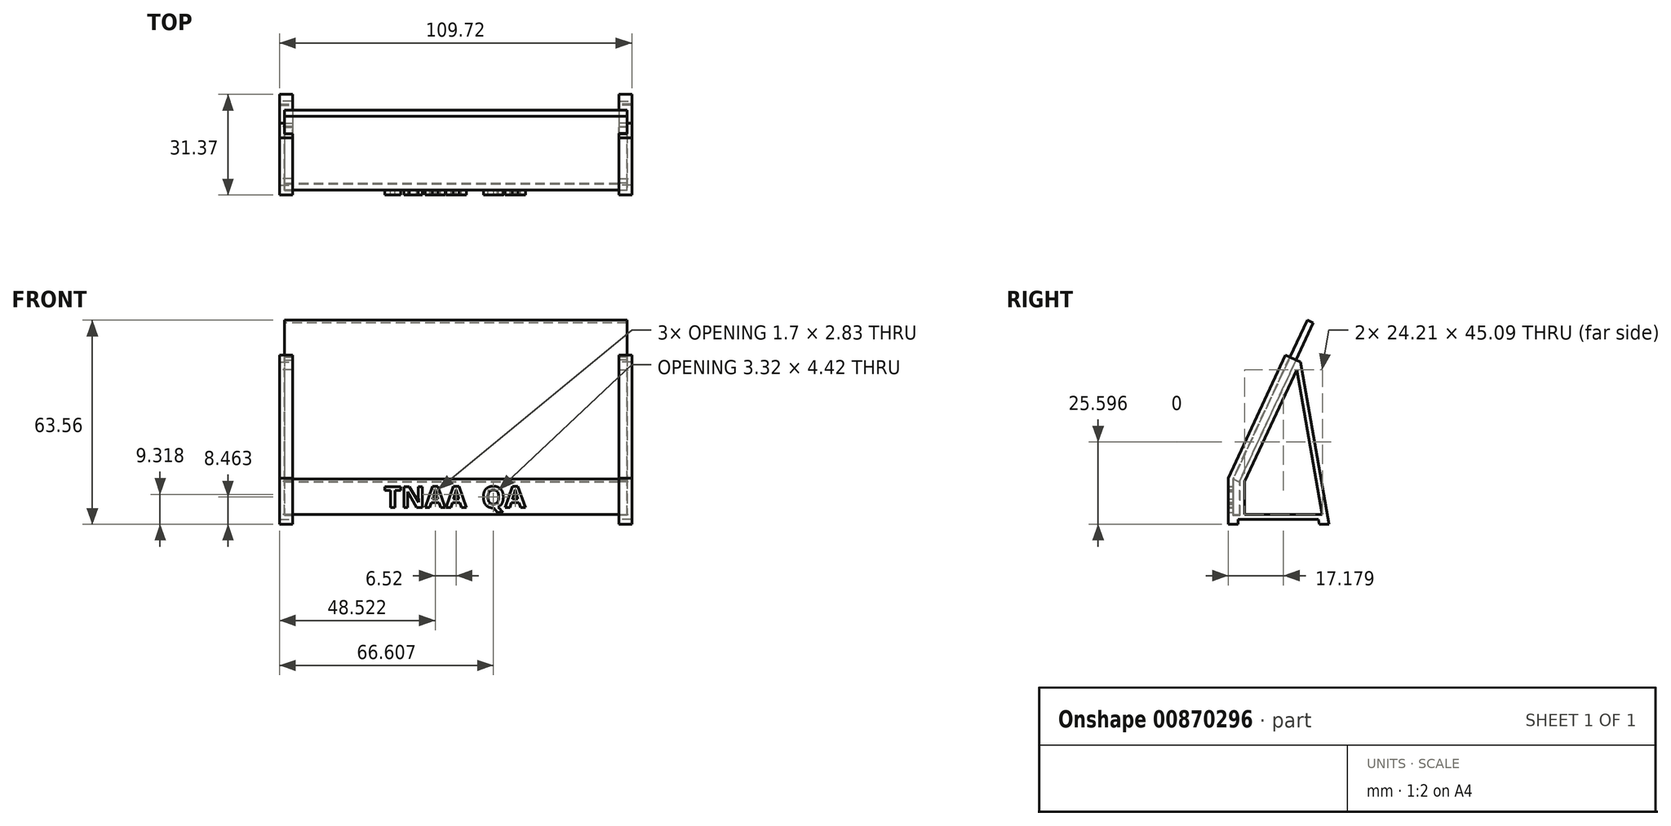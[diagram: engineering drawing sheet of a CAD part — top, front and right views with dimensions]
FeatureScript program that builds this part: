
annotation { "Feature Type Name" : "Feature", "Feature Type Description" : "" }
export const myFeature = defineFeature(function(context is Context, id is Id, definition is map)
    precondition{}
    {
        {
            var Q0;
            Q0=qCreatedBy(makeId("Right.planeOp"),FACE);
            var sketch = newSketch(context, id + "F0", { "sketchPlane" : qUnion([Q0])});
            skLineSegment(sketch, "E0", {"start": v(0, 49.5) * mm, "end": v(-23.08, 0) * mm});
            skLineSegment(sketch, "E1", {"start": v(0, 49.5) * mm, "end": v(-1.84, 50.35) * mm});
            skLineSegment(sketch, "E2", {"start": v(-1.84, 50.35) * mm, "end": v(-24.92, 0.86) * mm});
            skLineSegment(sketch, "E3", {"start": v(-24.92, 0.86) * mm, "end": v(-23.08, 0) * mm});
            skSolve(sketch);
        }
        {
            var Q0;
            Q0=qCreatedBy(makeId("Right.planeOp"),FACE);
            var sketch = newSketch(context, id + "F1", { "sketchPlane" : qUnion([Q0])});
            skLineSegment(sketch, "E4", {"start": v(-22.89, -0.09) * mm, "end": v(-24.92, 0.86) * mm});
            skLineSegment(sketch, "E5", {"start": v(-24.92, 0.86) * mm, "end": v(-24.92, -10.16) * mm});
            skLineSegment(sketch, "E6", {"start": v(-24.92, -10.16) * mm, "end": v(-22.89, -10.16) * mm});
            skLineSegment(sketch, "E7", {"start": v(-22.89, -10.16) * mm, "end": v(-22.89, -0.09) * mm});
            skSolve(sketch);
        }
        {
            var Q0;
            Q0=makeQuery(id+"F1.imprint","IMPRINT",FACE,{"disambiguationData":[TD([[makeQuery(id+"F1.imprint","IMPRINT",EDGE,{"derivedFrom":sQuery(id+"F1.wireOp",EDGE,"E4")}),1.0]])]});
            extrude(context, id + "F2", {"entities" : qUnion([Q0]), "endBound" : BoundingType.SYMMETRIC, "depth" : 106.68 * mm, "offsetDistance" : 25.4 * mm});
        }
        {
            var Q0;
            Q0=makeQuery(id+"F2.opExtrude","SWEPT_FACE",FACE,{"disambiguationData":[OSD([sQuery(id+"F1.wireOp",EDGE,"E5")])]});
            var sketch = newSketch(context, id + "F3", { "sketchPlane" : qUnion([Q0])});
            skText(sketch, "E8", { "text": "TNAA  QA", "fontName": "OpenSans-Bold.ttf"});
            const initialGuessF3  = {"E8": [-0.02227, -0.00803, 1, 0, 0.0066]};
            skSetInitialGuess(sketch, initialGuessF3);
            skSolve(sketch);
        }
        {
            var Q0;
            Q0 = qSketchRegion(id + "F3", true);
            extrude(context, id + "F4", {"entities" : qUnion([Q0]), "depth" : 1.52 * mm, "offsetDistance" : 25.4 * mm});
        }
        {
            var Q0;
            Q0=makeQuery(id+"F0.imprint","IMPRINT",FACE,{"disambiguationData":[TD([[makeQuery(id+"F0.imprint","IMPRINT",EDGE,{"derivedFrom":sQuery(id+"F0.wireOp",EDGE,"E0")}),-1.0]])]});
            extrude(context, id + "F5", {"entities" : qUnion([Q0]), "endBound" : BoundingType.SYMMETRIC, "depth" : 106.68 * mm, "offsetDistance" : 25.4 * mm});
        }
        {
            var Q0;
            Q0=makeQuery(id+"F5.opExtrude","CAP_FACE",FACE,{"disambiguationData":[OSD([sQuery(id+"F0.wireOp",EDGE,"E0"),sQuery(id+"F0.wireOp",EDGE,"E1"),sQuery(id+"F0.wireOp",EDGE,"E2"),sQuery(id+"F0.wireOp",EDGE,"E3")])],"isStart":false});
            cPlane(context, id + "F6", {"entities" : qUnion([Q0]), "cplaneType" : CPlaneType.OFFSET, "offset" : 2.54 * mm, "oppositeDirection" : true, "width" : 152.4 * mm, "height" : 152.4 * mm});
        }
        {
            var Q0;
            Q0=qCreatedBy(id+"F6.planeOp",FACE);
            var sketch = newSketch(context, id + "F7", { "sketchPlane" : qUnion([Q0])});
            skLineSegment(sketch, "E9", {"start": v(-3.99, 37.34) * mm, "end": v(-8.6, 39.49) * mm});
            skLineSegment(sketch, "E10", {"start": v(-8.6, 39.49) * mm, "end": v(-26.44, 1.2) * mm});
            skLineSegment(sketch, "E11", {"start": v(-26.44, 1.2) * mm, "end": v(-26.44, -13.2) * mm});
            skLineSegment(sketch, "E12", {"start": v(4.93, -13.2) * mm, "end": v(-3.99, 37.34) * mm});
            skLineSegment(sketch, "E13", {"start": v(-23.4, -13.2) * mm, "end": v(-23.4, -11.68) * mm});
            skLineSegment(sketch, "E14", {"start": v(-23.4, -11.68) * mm, "end": v(1.61, -11.68) * mm});
            skLineSegment(sketch, "E15", {"start": v(1.61, -11.68) * mm, "end": v(1.88, -13.2) * mm});
            skLineSegment(sketch, "E16", {"start": v(-26.44, -13.2) * mm, "end": v(-23.4, -13.2) * mm});
            skLineSegment(sketch, "E17", {"start": v(1.88, -13.2) * mm, "end": v(4.93, -13.2) * mm});
            skSolve(sketch);
        }
        {
            var Q0;
            Q0=makeQuery(id+"F7.imprint","IMPRINT",FACE,{"disambiguationData":[TD([[makeQuery(id+"F7.imprint","IMPRINT",EDGE,{"derivedFrom":sQuery(id+"F7.wireOp",EDGE,"E9")}),1.0]])]});
            extrude(context, id + "F8", {"entities" : qUnion([Q0]), "depth" : 4.06 * mm, "offsetDistance" : 25.4 * mm});
        }
        {
            var Q0;
            Q0=qCreatedBy(id+"F6.planeOp",FACE);
            var sketch = newSketch(context, id + "F9", { "sketchPlane" : qUnion([Q0])});
            skLineSegment(sketch, "E18", {"start": v(-7.32, 38.9) * mm, "end": v(-25.05, 0.89) * mm});
            skLineSegment(sketch, "E19", {"start": v(-25.05, 0.89) * mm, "end": v(-25.05, -10.41) * mm});
            skLineSegment(sketch, "E20", {"start": v(-25.05, -10.41) * mm, "end": v(-22.76, -10.41) * mm});
            skLineSegment(sketch, "E21", {"start": v(-22.76, -10.41) * mm, "end": v(-22.76, 0.38) * mm});
            skLineSegment(sketch, "E22", {"start": v(-22.76, 0.38) * mm, "end": v(-5.25, 37.93) * mm});
            skLineSegment(sketch, "E23", {"start": v(-5.25, 37.93) * mm, "end": v(-7.32, 38.9) * mm});
            skSolve(sketch);
        }
        {
            var Q0;
            Q0=makeQuery(id+"F9.imprint","IMPRINT",FACE,{"disambiguationData":[TD([[makeQuery(id+"F9.imprint","IMPRINT",EDGE,{"derivedFrom":sQuery(id+"F9.wireOp",EDGE,"swIpo9da-VBfc-vrre-W5kq-tgqSe28huMO8")}),1.0]])]});
            var Q1;
            Q1=makeQuery(id+"F9.imprint","IMPRINT",FACE,{"disambiguationData":[TD([[makeQuery(id+"F9.imprint","IMPRINT",EDGE,{"derivedFrom":sQuery(id+"F9.wireOp",EDGE,"E18")}),1.0]])]});
            extrude(context, id + "F10", {"entities" : qUnion([Q0, Q1]), "operationType" : NewBodyOperationType.REMOVE, "depth" : 2.54 * mm, "offsetDistance" : 25.4 * mm});
        }
        {
            var Q0;
            Q0=makeQuery(id+"F8.opExtrude","CAP_FACE",FACE,{"disambiguationData":[OSD([sQuery(id+"F7.wireOp",EDGE,"E9"),sQuery(id+"F7.wireOp",EDGE,"E10"),sQuery(id+"F7.wireOp",EDGE,"E11"),sQuery(id+"F7.wireOp",EDGE,"yu6qPxHr-p48B-kqw4-Z5bB-Xz7mgbtkeqfO"),sQuery(id+"F7.wireOp",EDGE,"E12")])],"isStart":false});
            var sketch = newSketch(context, id + "F11", { "sketchPlane" : qUnion([Q0])});
            skLineSegment(sketch, "E24", {"start": v(-5.1, 34.93) * mm, "end": v(-21.36, 0.07) * mm});
            skLineSegment(sketch, "E25", {"start": v(-21.36, 0.07) * mm, "end": v(-21.36, -10.16) * mm});
            skLineSegment(sketch, "E26", {"start": v(-21.36, -10.16) * mm, "end": v(2.84, -10.16) * mm});
            skLineSegment(sketch, "E27", {"start": v(2.84, -10.16) * mm, "end": v(-5.1, 34.93) * mm});
            skSolve(sketch);
        }
        {
            var Q0;
            Q0=makeQuery(id+"F11.imprint","IMPRINT",FACE,{"disambiguationData":[TD([[makeQuery(id+"F11.imprint","IMPRINT",EDGE,{"derivedFrom":sQuery(id+"F11.wireOp",EDGE,"E24")}),1.0]])]});
            extrude(context, id + "F12", {"entities" : qUnion([Q0]), "operationType" : NewBodyOperationType.REMOVE, "oppositeDirection" : true, "depth" : 25.4 * mm, "offsetDistance" : 25.4 * mm});
        }
        {
            var Q0;
            Q0=makeQuery(id+"F8.opExtrude","SWEPT_BODY",BODY,{"disambiguationData":[OSD([sQuery(id+"F7.wireOp",EDGE,"E9"),sQuery(id+"F7.wireOp",EDGE,"E10"),sQuery(id+"F7.wireOp",EDGE,"E11"),sQuery(id+"F7.wireOp",EDGE,"yu6qPxHr-p48B-kqw4-Z5bB-Xz7mgbtkeqfO"),sQuery(id+"F7.wireOp",EDGE,"E12")])]});
            var Q1;
            Q1=qCreatedBy(makeId("Right.planeOp"),FACE);
            mirror(context, id + "F13", {"entities" : qUnion([Q0]), "mirrorPlane" : qUnion([Q1])});
        }
    });
